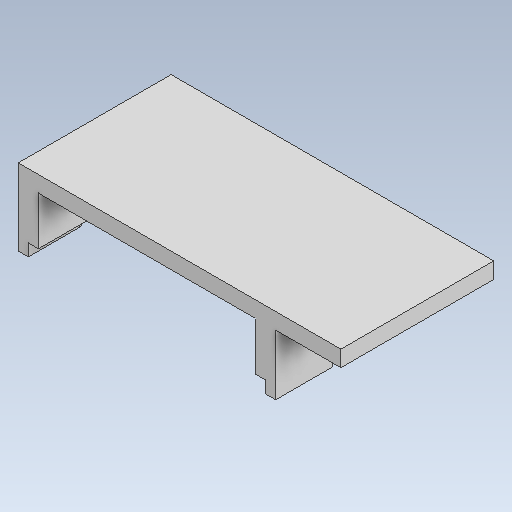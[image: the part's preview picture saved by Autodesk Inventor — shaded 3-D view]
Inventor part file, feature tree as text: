
AUTODESK INVENTOR PART (.ipt)
format: ipt  version: 2020.1 (Build 241239000, 239)  size: 143,872 bytes
history: native  units: mm
features: extrude x3, sketch x3, other x1
ambient origin geometry x8: Origin, YZ Plane, XZ Plane, XY Plane, X Axis, Y Axis, Z Axis, Center Point
bodies: Body1 (feature_tree)
feature tree (7):
  other  "Твердое тело1"
  extrude  "Выдавливание1"  Depth=15.0mm TaperAngle=0.0deg
  extrude  "Выдавливание2"  Depth=25.0mm
  extrude  "Выдавливание3"  Depth=25.0mm
  sketch  "Эскиз1"
  sketch  "Эскиз2"
  sketch  "Эскиз3"
